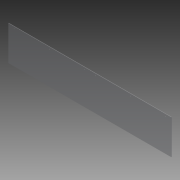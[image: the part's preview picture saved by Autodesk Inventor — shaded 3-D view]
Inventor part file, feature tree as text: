
AUTODESK INVENTOR PART (.ipt)
format: ipt  version: 2013 (Build 170138000, 138)  size: 84,992 bytes
history: native  units: in
note: dims shown in document units (in); Inventor stores cm internally (conversion verified against a paired STEP export)
features: sketch x2, extrude x1, hole x1
ambient origin geometry x8: Origin, YZ Plane, XZ Plane, XY Plane, X Axis, Y Axis, Z Axis, Center Point
bodies: Solid1 (feature_tree)
feature tree (4):
  extrude  "Extrusion1"  Depth=18.25in
  hole  "Hole1"  [1 undecoded]
  sketch  "Sketch1"  dims[d0=86.0in d1=18.25in]
  sketch  "Sketch2"  dims[d2=0.25in d3=0.0in d4=3.0in d5=1.0in d6=21.5in d7=40.0in d8=46.0in d9=64.5in d10=83.0in d11=0.38in d12=0.75in d13=0.375in d14=0.25in d15=0.5635in d16=1.0in d17=0.8108in]
note: 1 required parameter value undecoded (feature->parameter linkage not recoverable at this tier; creation-order binding heuristic only, values carry confidence <= 0.55)
